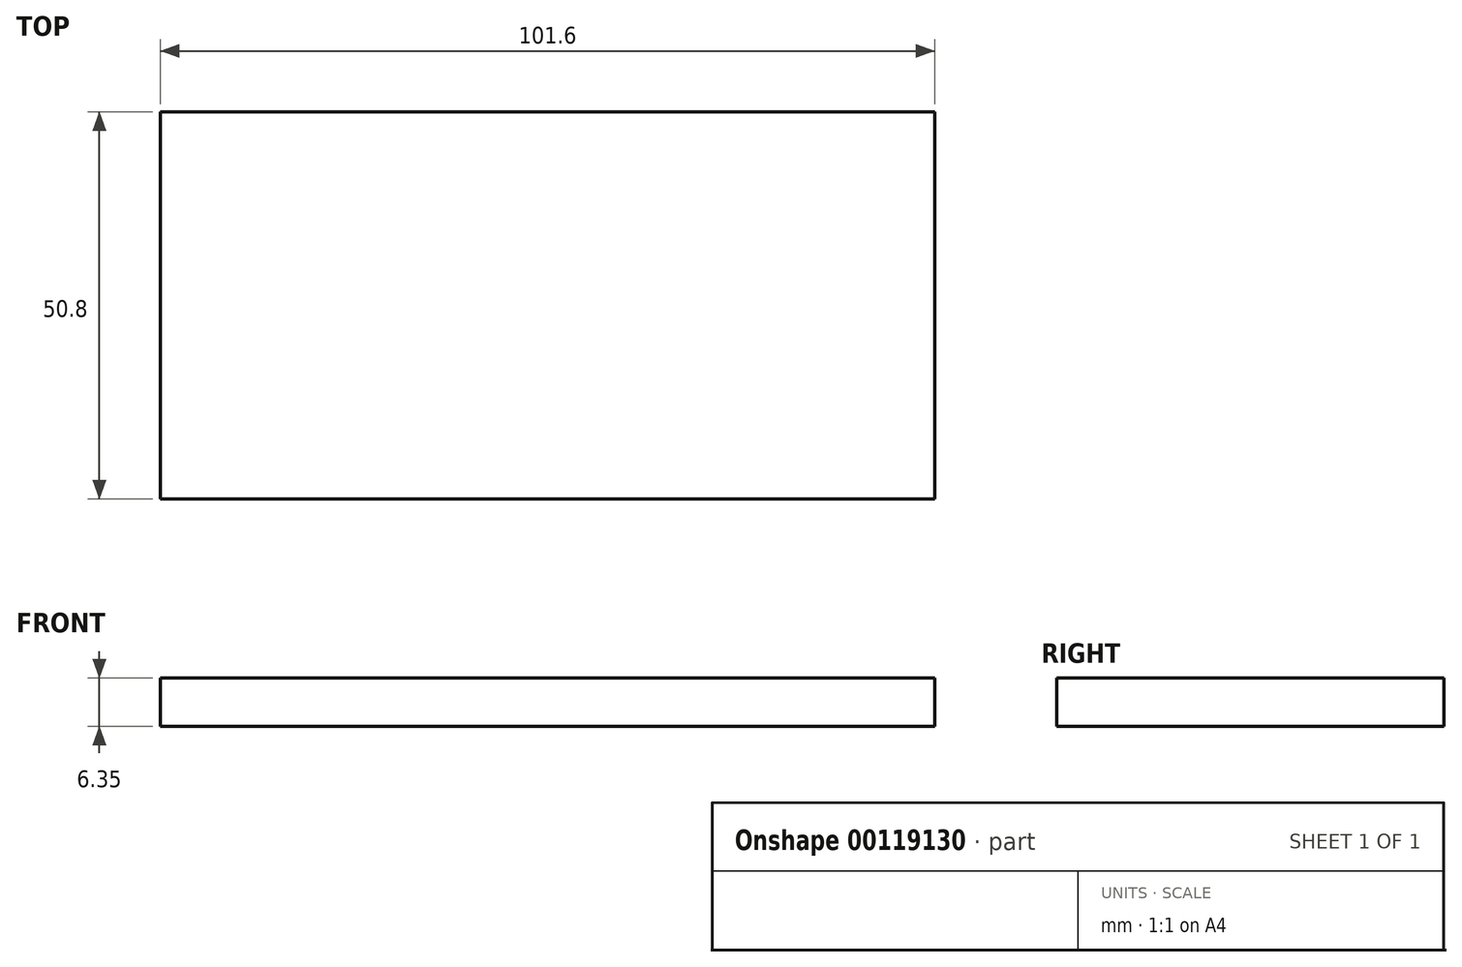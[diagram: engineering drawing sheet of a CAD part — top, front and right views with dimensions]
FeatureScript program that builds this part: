
annotation { "Feature Type Name" : "Feature", "Feature Type Description" : "" }
export const myFeature = defineFeature(function(context is Context, id is Id, definition is map)
    precondition{}
    {
        {
            var Q0;
            Q0=qCreatedBy(makeId("Top.planeOp"),FACE);
            var sketch = newSketch(context, id + "F0", { "sketchPlane" : qUnion([Q0])});
            skLineSegment(sketch, "E0.bottom", {"start": v(-50.8, 25.4) * mm, "end": v(50.8, 25.4) * mm});
            skLineSegment(sketch, "E0.top", {"start": v(-50.8, -25.4) * mm, "end": v(50.8, -25.4) * mm});
            skLineSegment(sketch, "E0.left", {"start": v(-50.8, 25.4) * mm, "end": v(-50.8, -25.4) * mm});
            skLineSegment(sketch, "E0.right", {"start": v(50.8, 25.4) * mm, "end": v(50.8, -25.4) * mm});
            skPoint(sketch, "E1", {"position": v(0, 25.4) * mm});
            skPoint(sketch, "E2", {"position": v(50.8, 0) * mm});
            skSolve(sketch);
        }
        {
            var Q0;
            Q0 = qSketchRegion(id + "F0", true);
            extrude(context, id + "F1", {"entities" : qUnion([Q0]), "depth" : 6.35 * mm});
        }
    });
